# Revit family: Shower-Valve_Trim-KOHLER-NATEO-K-18019IN1
name_source: partatom
category: Specialty Equipment
revit_build: Autodesk Revit 2017 (Build: 20160225_1515(x64)
units: mm (PartAtom-declared; Revit-internal decimal feet)

## family parameters
Cut with Voids When Loaded = No
Host = Face
OmniClass Number = 23.31.25.00
Part Type = Normal
Room Calculation Point = No
Round Connector Dimension = Use Diameter
Shared = No

## types (2) — shared parameters
ADA Compliant = No
Assembly Code = C1030200
Date Modified = 10/12/2020
Default Elevation = 42"
Finish = Kohler-Metal-CP-Polished_Chrome
Height = 8 1/8"
Length = 3 5/16"
Manufacturer = KOHLER Co.
Master Format 2014 = 10 28 00
Master Format 2014 Name = Toilet, Bath, and Laundry Accessories
Material = Premium Metal Construction
Product Name = NATEO
URL = https://www.kohler.co.in
WaterSense Certified = No
Width = 5 1/2"

## per-type parameters (varying)
| type | Description | Model | Product Documentation Link | Product Page URL | Type |
| CP- Polished Chrome | BATH AND SHOWER TRIM | K-18019IN-4-CP |  |  | 1 |
| FP, CP-Polished Chrome | Recessed bath and shower faucet trim with lever handle and diverter button | K-18019IN-4FP-CP | http://resources.kohler.com | https://www.kohler.co.in | 2 |

## geometry (parser evidence)
native form markers: Sweep x3
no freeform markers — native parametric forms only
